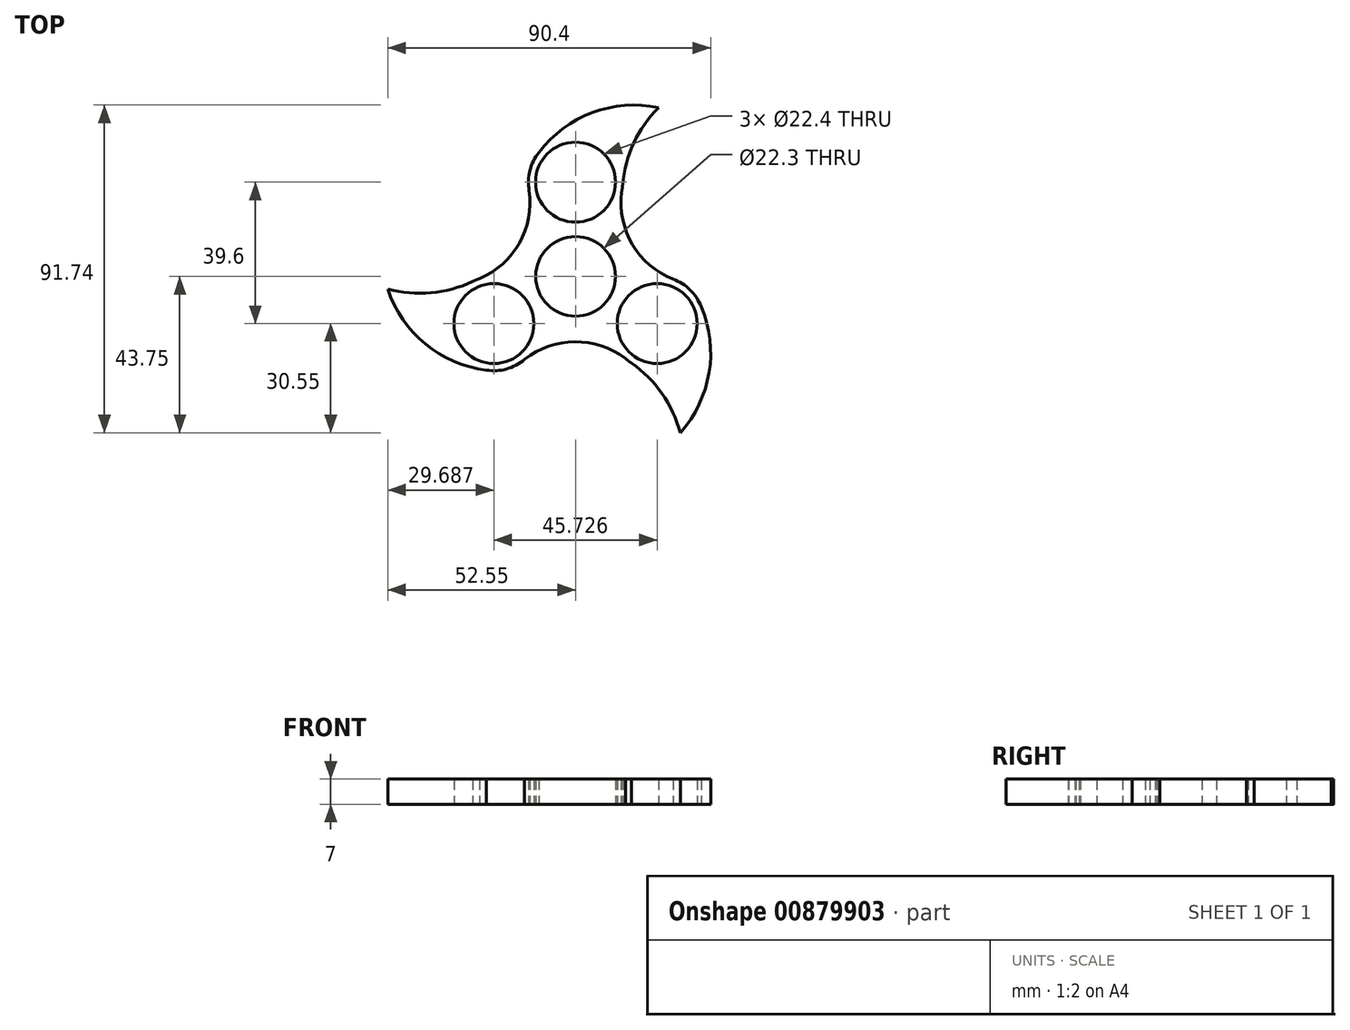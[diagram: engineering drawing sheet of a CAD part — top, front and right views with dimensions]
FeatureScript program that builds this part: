
annotation { "Feature Type Name" : "Feature", "Feature Type Description" : "" }
export const myFeature = defineFeature(function(context is Context, id is Id, definition is map)
    precondition{}
    {
        {
            var Q0;
            Q0=qCreatedBy(makeId("Top.planeOp"),FACE);
            var sketch = newSketch(context, id + "F0", { "sketchPlane" : qUnion([Q0])});
            skCircle(sketch, "E0", {"center": v(0, 0) * mm, "radius": 11.15 * mm});
            skArc(sketch, "E1", {"start": v(-10.25, 34.72) * mm, "mid": v(-12.79, 29.67) * mm, "end": v(-12.98, 24.02) * mm});
            skCircle(sketch, "E2", {"center": v(0, 26.4) * mm, "radius": 11.2 * mm});
            skCircle(sketch, "E3.1.0", {"center": v(-22.86, -13.2) * mm, "radius": 11.2 * mm});
            skArc(sketch, "E3.1.1", {"start": v(-26.89, -0.63) * mm, "mid": v(-27.87, -0.99) * mm, "end": v(-28.82, -1.42) * mm});
            skCircle(sketch, "E3.2.0", {"center": v(22.86, -13.2) * mm, "radius": 11.2 * mm});
            skArc(sketch, "E3.2.1", {"start": v(13.99, -22.97) * mm, "mid": v(14.79, -23.64) * mm, "end": v(15.64, -24.25) * mm});
            skArc(sketch, "E4", {"start": v(-28.33, -1.18) * mm, "mid": v(-15.96, 8.95) * mm, "end": v(-13.09, 24.67) * mm});
            skArc(sketch, "E5.1.0", {"start": v(15.19, -23.94) * mm, "mid": v(0.23, -18.3) * mm, "end": v(-14.82, -23.67) * mm});
            skArc(sketch, "E5.2.0", {"start": v(13.14, 25.12) * mm, "mid": v(15.73, 9.35) * mm, "end": v(27.91, -1) * mm});
            skArc(sketch, "E6", {"start": v(23.22, 47.27) * mm, "mid": v(4.66, 45.87) * mm, "end": v(-10.25, 34.72) * mm});
            skArc(sketch, "E7", {"start": v(23.22, 47.27) * mm, "mid": v(16.17, 37.11) * mm, "end": v(13.14, 25.12) * mm});
            skArc(sketch, "E8.1.0", {"start": v(-52.55, -3.52) * mm, "mid": v(-42.05, -18.9) * mm, "end": v(-24.94, -26.24) * mm});
            skArc(sketch, "E8.1.1", {"start": v(-52.55, -3.52) * mm, "mid": v(-40.23, -4.55) * mm, "end": v(-28.33, -1.18) * mm});
            skArc(sketch, "E8.2.0", {"start": v(29.33, -43.75) * mm, "mid": v(37.4, -26.97) * mm, "end": v(35.2, -8.48) * mm});
            skArc(sketch, "E8.2.1", {"start": v(29.33, -43.75) * mm, "mid": v(24.06, -32.56) * mm, "end": v(15.19, -23.94) * mm});
            skArc(sketch, "E9.trimOffspring", {"start": v(12.9, 23.6) * mm, "mid": v(13.08, 24.63) * mm, "end": v(13.18, 25.67) * mm});
            skArc(sketch, "E10.trimOffspring", {"start": v(-24.94, -26.24) * mm, "mid": v(-19.3, -25.9) * mm, "end": v(-14.3, -23.25) * mm});
            skArc(sketch, "E11.trimOffspring", {"start": v(35.2, -8.48) * mm, "mid": v(32.09, -3.76) * mm, "end": v(27.3, -0.77) * mm});
            skSolve(sketch);
        }
        {
            var Q0;
            Q0 = qSketchRegion(id + "F0", true);
            extrude(context, id + "F1", {"entities" : qUnion([Q0]), "depth" : 7 * mm, "offsetDistance" : 25 * mm});
        }
    });
